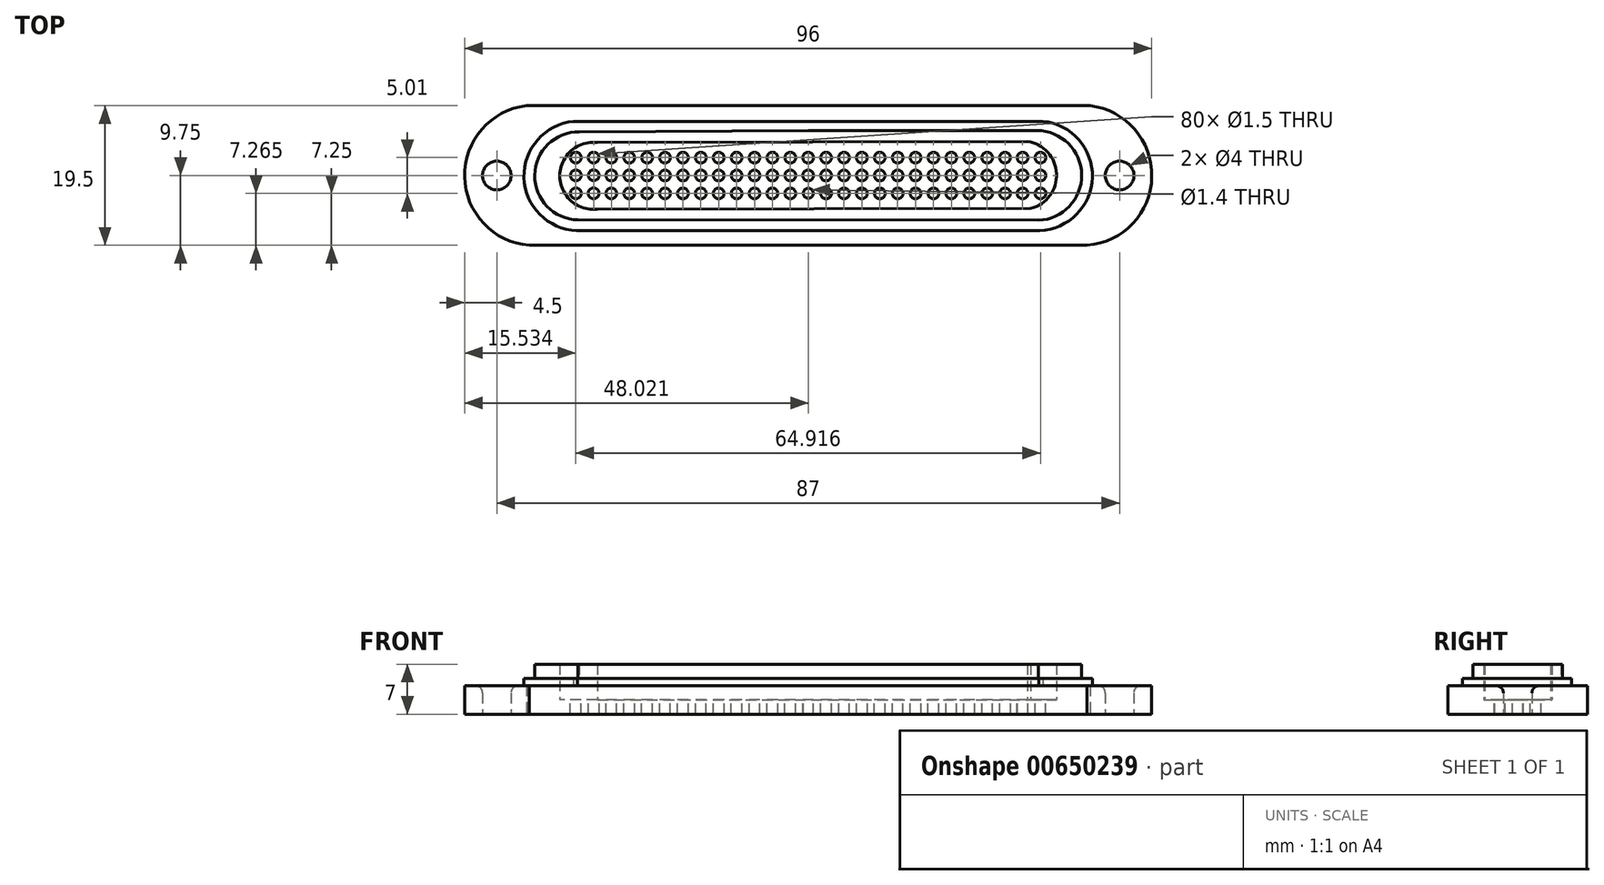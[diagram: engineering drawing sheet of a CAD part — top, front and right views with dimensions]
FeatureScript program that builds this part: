
annotation { "Feature Type Name" : "Feature", "Feature Type Description" : "" }
export const myFeature = defineFeature(function(context is Context, id is Id, definition is map)
    precondition{}
    {
        {
            var Q0;
            Q0=qCreatedBy(makeId("Top.planeOp"),FACE);
            var sketch = newSketch(context, id + "F0", { "sketchPlane" : qUnion([Q0])});
            skLineSegment(sketch, "E0.bottom", {"start": v(0, -9.75) * mm, "end": v(-38.98, -9.75) * mm});
            skLineSegment(sketch, "E0.top", {"start": v(0, 9.75) * mm, "end": v(-39.37, 9.75) * mm});
            skLineSegment(sketch, "E0.right", {"start": v(-48, 0) * mm, "end": v(-48, 0) * mm});
            skPoint(sketch, "E0.middle", {"position": v(0, 0) * mm});
            skArc(sketch, "E1", {"start": v(-39.37, 9.75) * mm, "mid": v(-48, -0.18) * mm, "end": v(-38.98, -9.75) * mm});
            skPoint(sketch, "E1.first.point", {"position": v(-38.98, -9.75) * mm});
            skPoint(sketch, "E1.second.point", {"position": v(-39.37, 9.75) * mm});
            skPoint(sketch, "E1.third.point", {"position": v(-48, 0) * mm});
            skLineSegment(sketch, "E2", {"start": v(0, 13.54) * mm, "end": v(0, -9.75) * mm, "construction": true});
            skPoint(sketch, "E3.orphan", {"position": v(-48, 9.75) * mm});
            skPoint(sketch, "E4.orphan", {"position": v(-48, -9.75) * mm});
            skPoint(sketch, "E0.left.end.orphan", {"position": v(48, 9.75) * mm});
            skPoint(sketch, "E0.left.start.orphan", {"position": v(48, -9.75) * mm});
            skLineSegment(sketch, "E5", {"start": v(-48, 0) * mm, "end": v(-43.5, 0) * mm, "construction": true});
            skCircle(sketch, "E6", {"center": v(-43.5, 0) * mm, "radius": 2 * mm});
            skLineSegment(sketch, "E7.MirrorCS", {"start": v(48, 0) * mm, "end": v(48, 0) * mm});
            skLineSegment(sketch, "E8.MirrorCS", {"start": v(48, 0) * mm, "end": v(43.5, 0) * mm, "construction": true});
            skPoint(sketch, "E9.MirrorP", {"position": v(39.37, 9.75) * mm});
            skArc(sketch, "E10.MirrorCS", {"start": v(39.37, 9.75) * mm, "mid": v(48, -0.18) * mm, "end": v(38.98, -9.75) * mm});
            skPoint(sketch, "E11.MirrorP", {"position": v(38.98, -9.75) * mm});
            skCircle(sketch, "E12.MirrorC", {"center": v(43.5, 0) * mm, "radius": 2 * mm});
            skPoint(sketch, "E13.MirrorP", {"position": v(48, 0) * mm});
            skLineSegment(sketch, "E14.MirrorCS", {"start": v(0, -9.75) * mm, "end": v(38.98, -9.75) * mm});
            skLineSegment(sketch, "E15.MirrorCS", {"start": v(0, 9.75) * mm, "end": v(39.37, 9.75) * mm});
            skLineSegment(sketch, "E16.4", {"start": v(0, 6.28) * mm, "end": v(31.95, 6.28) * mm});
            skLineSegment(sketch, "E16.5", {"start": v(0, 6.28) * mm, "end": v(-31.98, 6.1) * mm});
            skArc(sketch, "E17", {"start": v(-31.98, 6.1) * mm, "mid": v(-38.2, 0.04) * mm, "end": v(-32.17, -6.2) * mm});
            skArc(sketch, "E18", {"start": v(32.16, -6.25) * mm, "mid": v(38.2, 0.11) * mm, "end": v(31.95, 6.28) * mm});
            skArc(sketch, "E19.0", {"start": v(-32.79, 7.56) * mm, "mid": v(-39.7, -0.28) * mm, "end": v(-32.34, -7.69) * mm});
            skArc(sketch, "E20.MirrorCS", {"start": v(32.79, 7.56) * mm, "mid": v(39.7, -0.28) * mm, "end": v(32.34, -7.69) * mm});
            skLineSegment(sketch, "E21", {"start": v(-32.34, -7.69) * mm, "end": v(-32.2, -7.7) * mm});
            skLineSegment(sketch, "E22", {"start": v(32.2, -7.7) * mm, "end": v(32.34, -7.69) * mm});
            skLineSegment(sketch, "E23", {"start": v(-38.2, 0.02) * mm, "end": v(-34.7, 0.02) * mm, "construction": true});
            skArc(sketch, "E24", {"start": v(-29.44, 4.61) * mm, "mid": v(-34.7, -0.05) * mm, "end": v(-29.44, -4.7) * mm});
            skLineSegment(sketch, "E25", {"start": v(38.2, 0.02) * mm, "end": v(34.7, 0.02) * mm, "construction": true});
            skArc(sketch, "E26", {"start": v(31.1, -4.6) * mm, "mid": v(34.7, 0.27) * mm, "end": v(30.64, 4.78) * mm});
            skLineSegment(sketch, "E27", {"start": v(-29.44, -4.7) * mm, "end": v(31.1, -4.6) * mm});
            skLineSegment(sketch, "E28", {"start": v(-32.17, -6.2) * mm, "end": v(32.16, -6.25) * mm});
            skLineSegment(sketch, "E29", {"start": v(-32.79, 7.56) * mm, "end": v(32.79, 7.56) * mm});
            skLineSegment(sketch, "E30", {"start": v(-32.2, -7.7) * mm, "end": v(32.2, -7.7) * mm});
            skLineSegment(sketch, "E31", {"start": v(-29.44, 4.61) * mm, "end": v(30.64, 4.78) * mm});
            skSolve(sketch);
        }
        {
            var Q0;
            Q0=qSketchRegion(id+"F0",true);
            extrude(context, id + "F1", {"entities" : qUnion([Q0]), "depth" : 4 * mm, "offsetDistance" : 25 * mm});
        }
        {
            var Q0;
            Q0=makeQuery(id+"F0.imprint","IMPRINT",FACE,{"disambiguationData":[TD([[makeQuery(id+"F0.imprint","IMPRINT",EDGE,{"derivedFrom":sQuery(id+"F0.wireOp",EDGE,"E16.4")}),1.0]])]});
            extrude(context, id + "F2", {"entities" : qUnion([Q0]), "operationType" : NewBodyOperationType.ADD, "depth" : 5 * mm, "offsetDistance" : 25 * mm});
        }
        {
            var Q0;
            Q0=makeQuery(id+"F0.imprint","IMPRINT",FACE,{"disambiguationData":[TD([[makeQuery(id+"F0.imprint","IMPRINT",EDGE,{"derivedFrom":sQuery(id+"F0.wireOp",EDGE,"E16.4")}),-1.0]])]});
            extrude(context, id + "F3", {"entities" : qUnion([Q0]), "operationType" : NewBodyOperationType.ADD, "depth" : 7 * mm, "offsetDistance" : 25 * mm});
        }
        {
            var Q0;
            Q0=makeQuery(id+"F0.imprint","IMPRINT",FACE,{"disambiguationData":[TD([[makeQuery(id+"F0.imprint","IMPRINT",EDGE,{"derivedFrom":sQuery(id+"F0.wireOp",EDGE,"E24")}),1.0]])]});
            extrude(context, id + "F4", {"entities" : qUnion([Q0]), "operationType" : NewBodyOperationType.ADD, "depth" : 2 * mm, "offsetDistance" : 25 * mm});
        }
        {
            var Q0;
            Q0=makeQuery(id+"F4.opExtrude","CAP_FACE",FACE,{"disambiguationData":[OSD([sQuery(id+"F0.wireOp",EDGE,"E24"),sQuery(id+"F0.wireOp",EDGE,"E26"),sQuery(id+"F0.wireOp",EDGE,"E27"),sQuery(id+"F0.wireOp",EDGE,"E31")])],"isStart":false});
            var sketch = newSketch(context, id + "F5", { "sketchPlane" : qUnion([Q0])});
            skArc(sketch, "E32", {"start": v(0, -0.75) * mm, "mid": v(0.75, 0) * mm, "end": v(0, 0.75) * mm});
            skArc(sketch, "E33.0.1.0", {"start": v(0, 1.75) * mm, "mid": v(0.75, 2.5) * mm, "end": v(0, 3.25) * mm});
            skCircle(sketch, "E33.1.0.0", {"center": v(2.5, 0) * mm, "radius": 0.75 * mm});
            skCircle(sketch, "E33.1.1.0", {"center": v(2.5, 2.5) * mm, "radius": 0.75 * mm});
            skCircle(sketch, "E33.2.0.0", {"center": v(5, 0) * mm, "radius": 0.75 * mm});
            skCircle(sketch, "E33.2.1.0", {"center": v(5, 2.5) * mm, "radius": 0.75 * mm});
            skCircle(sketch, "E33.3.0.0", {"center": v(7.5, 0) * mm, "radius": 0.75 * mm});
            skCircle(sketch, "E33.3.1.0", {"center": v(7.5, 2.5) * mm, "radius": 0.75 * mm});
            skCircle(sketch, "E33.4.0.0", {"center": v(10, 0) * mm, "radius": 0.75 * mm});
            skCircle(sketch, "E33.4.1.0", {"center": v(10, 2.5) * mm, "radius": 0.75 * mm});
            skCircle(sketch, "E33.5.0.0", {"center": v(12.5, 0) * mm, "radius": 0.75 * mm});
            skCircle(sketch, "E33.5.1.0", {"center": v(12.5, 2.5) * mm, "radius": 0.75 * mm});
            skCircle(sketch, "E33.6.0.0", {"center": v(15, 0) * mm, "radius": 0.75 * mm});
            skCircle(sketch, "E33.6.1.0", {"center": v(15, 2.5) * mm, "radius": 0.75 * mm});
            skCircle(sketch, "E33.7.0.0", {"center": v(17.5, 0) * mm, "radius": 0.75 * mm});
            skCircle(sketch, "E33.7.1.0", {"center": v(17.5, 2.5) * mm, "radius": 0.75 * mm});
            skCircle(sketch, "E33.8.0.0", {"center": v(20, 0) * mm, "radius": 0.75 * mm});
            skCircle(sketch, "E33.8.1.0", {"center": v(20, 2.5) * mm, "radius": 0.75 * mm});
            skCircle(sketch, "E33.9.0.0", {"center": v(22.5, 0) * mm, "radius": 0.75 * mm});
            skCircle(sketch, "E33.9.1.0", {"center": v(22.5, 2.5) * mm, "radius": 0.75 * mm});
            skCircle(sketch, "E33.10.0.0", {"center": v(25, 0) * mm, "radius": 0.75 * mm});
            skCircle(sketch, "E33.10.1.0", {"center": v(25, 2.5) * mm, "radius": 0.75 * mm});
            skCircle(sketch, "E33.11.0.0", {"center": v(27.5, 0) * mm, "radius": 0.75 * mm});
            skCircle(sketch, "E33.11.1.0", {"center": v(27.5, 2.5) * mm, "radius": 0.75 * mm});
            skLineSegment(sketch, "E33.direction1", {"start": v(0, 0) * mm, "end": v(2.5, 0) * mm, "construction": true});
            skLineSegment(sketch, "E33.direction2", {"start": v(0, 0) * mm, "end": v(0, 2.5) * mm, "construction": true});
            skLineSegment(sketch, "E34", {"start": v(0, 4) * mm, "end": v(0, -4) * mm, "construction": true});
            skCircle(sketch, "E35.0.1.0", {"center": v(2.5, -2.5) * mm, "radius": 0.75 * mm});
            skCircle(sketch, "E35.1.1.0", {"center": v(5, -2.5) * mm, "radius": 0.75 * mm});
            skCircle(sketch, "E35.2.1.0", {"center": v(7.5, -2.5) * mm, "radius": 0.75 * mm});
            skCircle(sketch, "E35.3.1.0", {"center": v(10, -2.5) * mm, "radius": 0.75 * mm});
            skCircle(sketch, "E35.4.1.0", {"center": v(12.5, -2.5) * mm, "radius": 0.75 * mm});
            skCircle(sketch, "E35.5.1.0", {"center": v(15, -2.5) * mm, "radius": 0.75 * mm});
            skCircle(sketch, "E35.6.1.0", {"center": v(17.5, -2.5) * mm, "radius": 0.75 * mm});
            skCircle(sketch, "E35.7.1.0", {"center": v(20, -2.5) * mm, "radius": 0.75 * mm});
            skCircle(sketch, "E35.8.1.0", {"center": v(22.5, -2.5) * mm, "radius": 0.75 * mm});
            skCircle(sketch, "E35.9.1.0", {"center": v(25, -2.5) * mm, "radius": 0.75 * mm});
            skCircle(sketch, "E35.10.1.0", {"center": v(27.5, -2.5) * mm, "radius": 0.75 * mm});
            skLineSegment(sketch, "E35.direction1", {"start": v(2.5, 0) * mm, "end": v(5, 0) * mm, "construction": true});
            skLineSegment(sketch, "E35.direction2", {"start": v(2.5, 0) * mm, "end": v(2.5, -2.5) * mm, "construction": true});
            skArc(sketch, "E36.MirrorCS", {"start": v(0, 1.75) * mm, "mid": v(-0.75, 2.5) * mm, "end": v(0, 3.25) * mm});
            skCircle(sketch, "E37.MirrorC", {"center": v(-12.5, 0) * mm, "radius": 0.75 * mm});
            skCircle(sketch, "E38.MirrorC", {"center": v(-17.5, 0) * mm, "radius": 0.75 * mm});
            skCircle(sketch, "E39.MirrorC", {"center": v(-7.5, 0) * mm, "radius": 0.75 * mm});
            skCircle(sketch, "E40.MirrorC", {"center": v(-5, 0) * mm, "radius": 0.75 * mm});
            skCircle(sketch, "E41.MirrorC", {"center": v(-15, 0) * mm, "radius": 0.75 * mm});
            skCircle(sketch, "E42.MirrorC", {"center": v(-20, 0) * mm, "radius": 0.75 * mm});
            skCircle(sketch, "E43.MirrorC", {"center": v(-10, 0) * mm, "radius": 0.75 * mm});
            skCircle(sketch, "E44.MirrorC", {"center": v(-12.5, 2.5) * mm, "radius": 0.75 * mm});
            skCircle(sketch, "E45.MirrorC", {"center": v(-10, 2.5) * mm, "radius": 0.75 * mm});
            skCircle(sketch, "E46.MirrorC", {"center": v(-7.5, 2.5) * mm, "radius": 0.75 * mm});
            skCircle(sketch, "E47.MirrorC", {"center": v(-5, 2.5) * mm, "radius": 0.75 * mm});
            skCircle(sketch, "E48.MirrorC", {"center": v(-2.5, 0) * mm, "radius": 0.75 * mm});
            skCircle(sketch, "E49.MirrorC", {"center": v(-2.5, 2.5) * mm, "radius": 0.75 * mm});
            skArc(sketch, "E50.MirrorCS", {"start": v(0, -0.75) * mm, "mid": v(-0.75, 0) * mm, "end": v(0, 0.75) * mm});
            skCircle(sketch, "E51.MirrorC", {"center": v(-17.5, 2.5) * mm, "radius": 0.75 * mm});
            skCircle(sketch, "E52.MirrorC", {"center": v(-15, 2.5) * mm, "radius": 0.75 * mm});
            skLineSegment(sketch, "E53.MirrorCS", {"start": v(0, 0) * mm, "end": v(-2.5, 0) * mm, "construction": true});
            skCircle(sketch, "E54.MirrorC", {"center": v(-20, 2.5) * mm, "radius": 0.75 * mm});
            skLineSegment(sketch, "E55.MirrorCS", {"start": v(-2.5, 0) * mm, "end": v(-2.5, -2.5) * mm, "construction": true});
            skLineSegment(sketch, "E56.MirrorCS", {"start": v(-2.5, 0) * mm, "end": v(-5, 0) * mm, "construction": true});
            skCircle(sketch, "E57.MirrorC", {"center": v(-27.5, 0) * mm, "radius": 0.75 * mm});
            skCircle(sketch, "E58.MirrorC", {"center": v(-22.5, 0) * mm, "radius": 0.75 * mm});
            skCircle(sketch, "E59.MirrorC", {"center": v(-25, 0) * mm, "radius": 0.75 * mm});
            skCircle(sketch, "E60.MirrorC", {"center": v(-27.5, -2.5) * mm, "radius": 0.75 * mm});
            skCircle(sketch, "E61.MirrorC", {"center": v(-25, 2.5) * mm, "radius": 0.75 * mm});
            skCircle(sketch, "E62.MirrorC", {"center": v(-22.5, 2.5) * mm, "radius": 0.75 * mm});
            skCircle(sketch, "E63.MirrorC", {"center": v(-17.5, -2.5) * mm, "radius": 0.75 * mm});
            skCircle(sketch, "E64.MirrorC", {"center": v(-27.5, 2.5) * mm, "radius": 0.75 * mm});
            skCircle(sketch, "E65.MirrorC", {"center": v(-20, -2.5) * mm, "radius": 0.75 * mm});
            skCircle(sketch, "E66.MirrorC", {"center": v(-22.5, -2.5) * mm, "radius": 0.75 * mm});
            skCircle(sketch, "E67.MirrorC", {"center": v(-25, -2.5) * mm, "radius": 0.75 * mm});
            skCircle(sketch, "E68.MirrorC", {"center": v(-2.5, -2.5) * mm, "radius": 0.75 * mm});
            skCircle(sketch, "E69.MirrorC", {"center": v(-5, -2.5) * mm, "radius": 0.75 * mm});
            skCircle(sketch, "E70.MirrorC", {"center": v(-7.5, -2.5) * mm, "radius": 0.75 * mm});
            skCircle(sketch, "E71.MirrorC", {"center": v(-10, -2.5) * mm, "radius": 0.75 * mm});
            skCircle(sketch, "E72.MirrorC", {"center": v(-12.5, -2.5) * mm, "radius": 0.75 * mm});
            skCircle(sketch, "E73.MirrorC", {"center": v(-15, -2.5) * mm, "radius": 0.75 * mm});
            skCircle(sketch, "E74.0.1.0", {"center": v(0.02, -2.49) * mm, "radius": 0.7 * mm});
            skLineSegment(sketch, "E75", {"start": v(-27.5, 0) * mm, "end": v(-30, 0) * mm, "construction": true});
            skCircle(sketch, "E76.MirrorC", {"center": v(-29.96, 0.04) * mm, "radius": 0.75 * mm});
            skCircle(sketch, "E77.MirrorC", {"center": v(29.96, 0.04) * mm, "radius": 0.75 * mm});
            skCircle(sketch, "E78.9.1.0", {"center": v(29.95, 2.5) * mm, "radius": 0.75 * mm});
            skCircle(sketch, "E78.10.1.0", {"center": v(32.45, 2.5) * mm, "radius": 0.75 * mm});
            skCircle(sketch, "E79.8.1.0", {"center": v(29.95, -2.5) * mm, "radius": 0.75 * mm});
            skCircle(sketch, "E79.9.0.0", {"center": v(32.45, 0) * mm, "radius": 0.75 * mm});
            skCircle(sketch, "E79.9.1.0", {"center": v(32.45, -2.5) * mm, "radius": 0.75 * mm});
            skCircle(sketch, "E80.MirrorC", {"center": v(-32.47, 0) * mm, "radius": 0.75 * mm});
            skCircle(sketch, "E81.MirrorC", {"center": v(-32.47, -2.5) * mm, "radius": 0.75 * mm});
            skCircle(sketch, "E82.MirrorC", {"center": v(-29.97, 2.5) * mm, "radius": 0.75 * mm});
            skCircle(sketch, "E83.MirrorC", {"center": v(-32.47, 2.5) * mm, "radius": 0.75 * mm});
            skCircle(sketch, "E84.MirrorC", {"center": v(-29.97, -2.5) * mm, "radius": 0.75 * mm});
            skSolve(sketch);
        }
        {
            var Q0;
            Q0=qSketchRegion(id+"F5",true);
            extrude(context, id + "F6", {"entities" : qUnion([Q0]), "operationType" : NewBodyOperationType.REMOVE, "oppositeDirection" : true, "depth" : 25 * mm, "offsetDistance" : 25 * mm});
        }
        {
            var Q0;
            Q0=makeQuery(id+"F1.opExtrude","CAP_EDGE",EDGE,{"disambiguationData":[OSD([sQuery(id+"F0.wireOp",EDGE,"E6")])],"isStart":false});
            var Q1;
            Q1=makeQuery(id+"F1.opExtrude","CAP_EDGE",EDGE,{"disambiguationData":[OSD([sQuery(id+"F0.wireOp",EDGE,"E12.MirrorC")])],"isStart":false});
            fillet(context, id + "F7", {"entities" : qUnion([Q0, Q1]), "radius" : 1 * mm, "tangentPropagation" : true, "allowEdgeOverflow" : false});
        }
    });
